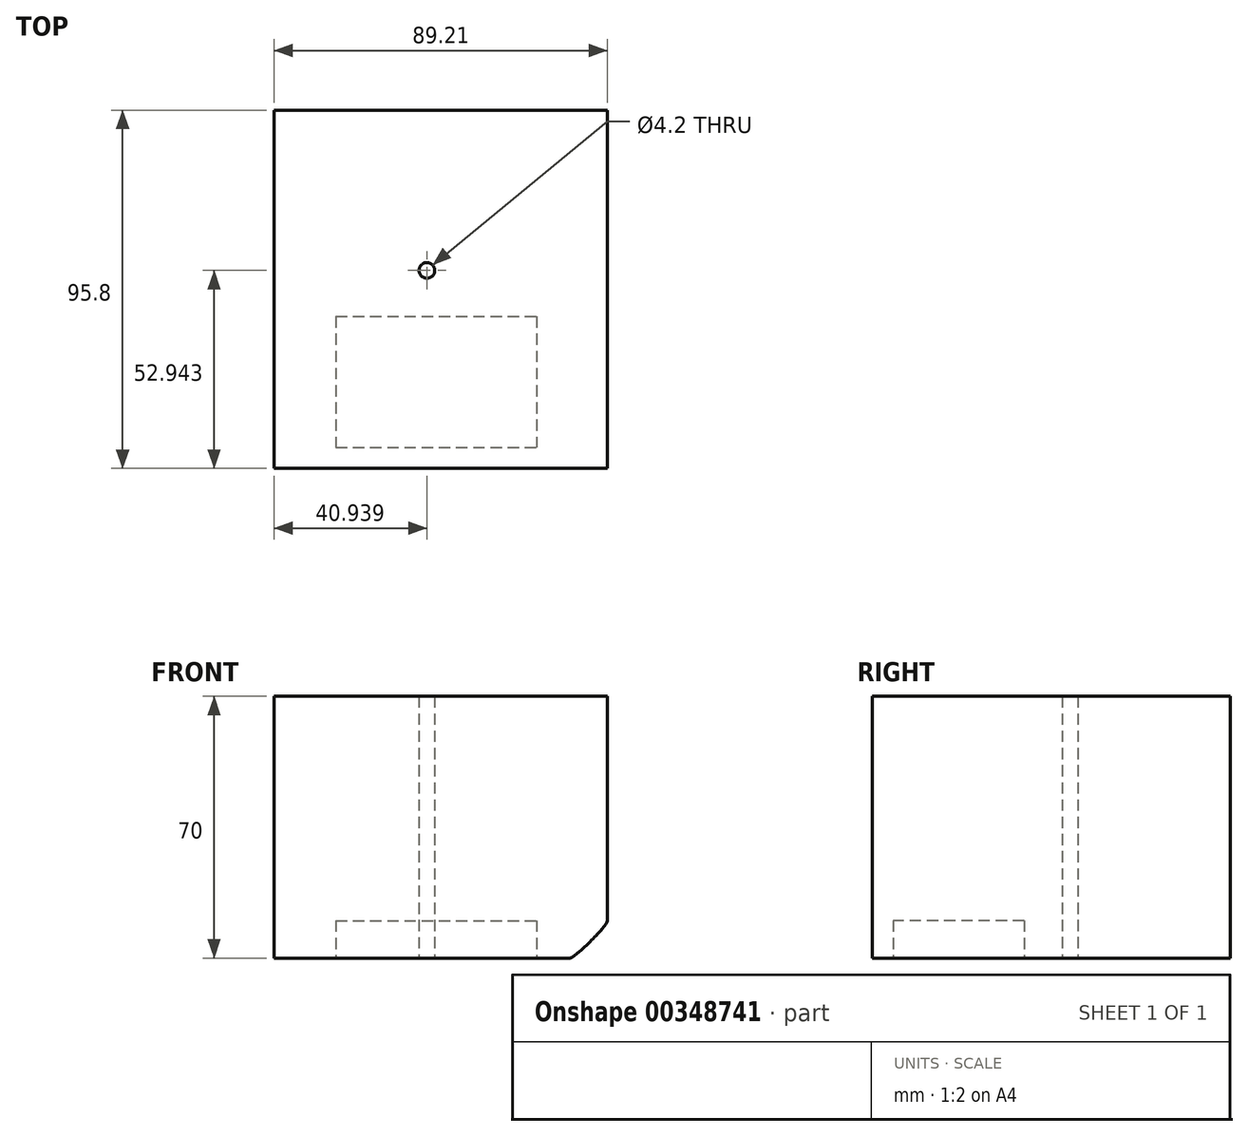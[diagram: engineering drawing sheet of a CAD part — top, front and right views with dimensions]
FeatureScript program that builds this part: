
annotation { "Feature Type Name" : "Feature", "Feature Type Description" : "" }
export const myFeature = defineFeature(function(context is Context, id is Id, definition is map)
    precondition{}
    {
        {
            var Q0;
            Q0=qCreatedBy(makeId("Top.planeOp"),FACE);
            var sketch = newSketch(context, id + "F0", { "sketchPlane" : qUnion([Q0])});
            skLineSegment(sketch, "E0.bottom", {"start": v(0, 0) * mm, "end": v(89.21, 0) * mm});
            skLineSegment(sketch, "E0.top", {"start": v(0, 95.8) * mm, "end": v(89.21, 95.8) * mm});
            skLineSegment(sketch, "E0.left", {"start": v(0, 0) * mm, "end": v(0, 95.8) * mm});
            skLineSegment(sketch, "E0.right", {"start": v(89.21, 0) * mm, "end": v(89.21, 95.8) * mm});
            skSolve(sketch);
        }
        {
            var Q0;
            Q0=makeQuery(id+"F0.imprint","IMPRINT",FACE,{"disambiguationData":[TD([[makeQuery(id+"F0.imprint","IMPRINT",EDGE,{"derivedFrom":sQuery(id+"F0.wireOp",EDGE,"E0.bottom")}),1.0]])]});
            extrude(context, id + "F1", {"entities" : qUnion([Q0]), "oppositeDirection" : true, "depth" : 20 * mm, "hasSecondDirection" : true, "secondDirectionOppositeDirection" : false, "secondDirectionDepth" : 50 * mm});
        }
        {
            var Q0;
            Q0=makeQuery(id+"F1.opExtrude","CAP_EDGE",EDGE,{"disambiguationData":[OSD([sQuery(id+"F0.wireOp",EDGE,"E0.right")])],"isStart":false});
            fillet(context, id + "F2", {"entities" : qUnion([Q0]), "radius" : 10 * mm, "tangentPropagation" : true, "rho" : 0.1, "crossSection" : FilletCrossSection.CONIC, "allowEdgeOverflow" : false});
        }
        {
            var Q0;
            Q0=makeQuery(id+"F1.opExtrude","CAP_FACE",FACE,{"disambiguationData":[OSD([sQuery(id+"F0.wireOp",EDGE,"E0.bottom"),sQuery(id+"F0.wireOp",EDGE,"E0.top"),sQuery(id+"F0.wireOp",EDGE,"E0.left"),sQuery(id+"F0.wireOp",EDGE,"E0.right")])],"isStart":false});
            var sketch = newSketch(context, id + "F3", { "sketchPlane" : qUnion([Q0])});
            skPoint(sketch, "E1", {"position": v(40.94, -52.94) * mm});
            skSolve(sketch);
        }
        {
            var Q0;
            Q0=sQuery(id+"F3.wireOp",VERTEX,"E1");
            var Q1;
            Q1=makeQuery(id+"F1.opExtrude","SWEPT_BODY",BODY,{"disambiguationData":[OSD([sQuery(id+"F0.wireOp",EDGE,"E0.bottom"),sQuery(id+"F0.wireOp",EDGE,"E0.top"),sQuery(id+"F0.wireOp",EDGE,"E0.left"),sQuery(id+"F0.wireOp",EDGE,"E0.right")])]});
            hole(context, id + "F4", {"style" : HoleStyle.SIMPLE, "endStyle" : HoleEndStyle.THROUGH, "standardTappedOrClearance" : lookupTablePath({ "standard" : "ISO", "engagement" : "75%", "pitch" : "0.8 mm", "size" : "M5", "type" : "Tapped" }), "standardBlindInLast" : lookupTablePath({ "standard" : "ISO", "engagement" : "75%", "pitch" : "0.8 mm", "size" : "M5", "type" : "Tapped" }), "holeDiameter" : 4.2 * mm, "showTappedDepth" : true, "isTappedThrough" : true, "tappedDepth" : 12 * mm, "tapClearance" : 3, "locations" : qUnion([Q0]), "scope" : qUnion([Q1]), "majorDiameter" : 5 * mm});
        }
        {
            var Q0;
            Q0=makeQuery(id+"F1.opExtrude","CAP_FACE",FACE,{"disambiguationData":[OSD([sQuery(id+"F0.wireOp",EDGE,"E0.bottom"),sQuery(id+"F0.wireOp",EDGE,"E0.top"),sQuery(id+"F0.wireOp",EDGE,"E0.left"),sQuery(id+"F0.wireOp",EDGE,"E0.right")])],"isStart":false});
            var sketch = newSketch(context, id + "F5", { "sketchPlane" : qUnion([Q0])});
            skLineSegment(sketch, "E2.bottom", {"start": v(16.56, -40.65) * mm, "end": v(70.26, -40.65) * mm});
            skLineSegment(sketch, "E2.top", {"start": v(16.56, -5.62) * mm, "end": v(70.26, -5.62) * mm});
            skLineSegment(sketch, "E2.left", {"start": v(16.56, -40.65) * mm, "end": v(16.56, -5.62) * mm});
            skLineSegment(sketch, "E2.right", {"start": v(70.26, -40.65) * mm, "end": v(70.26, -5.62) * mm});
            skSolve(sketch);
        }
        {
            var Q0;
            Q0=makeQuery(id+"F5.imprint","IMPRINT",FACE,{"disambiguationData":[TD([[makeQuery(id+"F5.imprint","IMPRINT",EDGE,{"derivedFrom":sQuery(id+"F5.wireOp",EDGE,"E2.bottom")}),1.0]])]});
            extrude(context, id + "F6", {"entities" : qUnion([Q0]), "operationType" : NewBodyOperationType.REMOVE, "oppositeDirection" : true, "depth" : 10 * mm});
        }
    });
